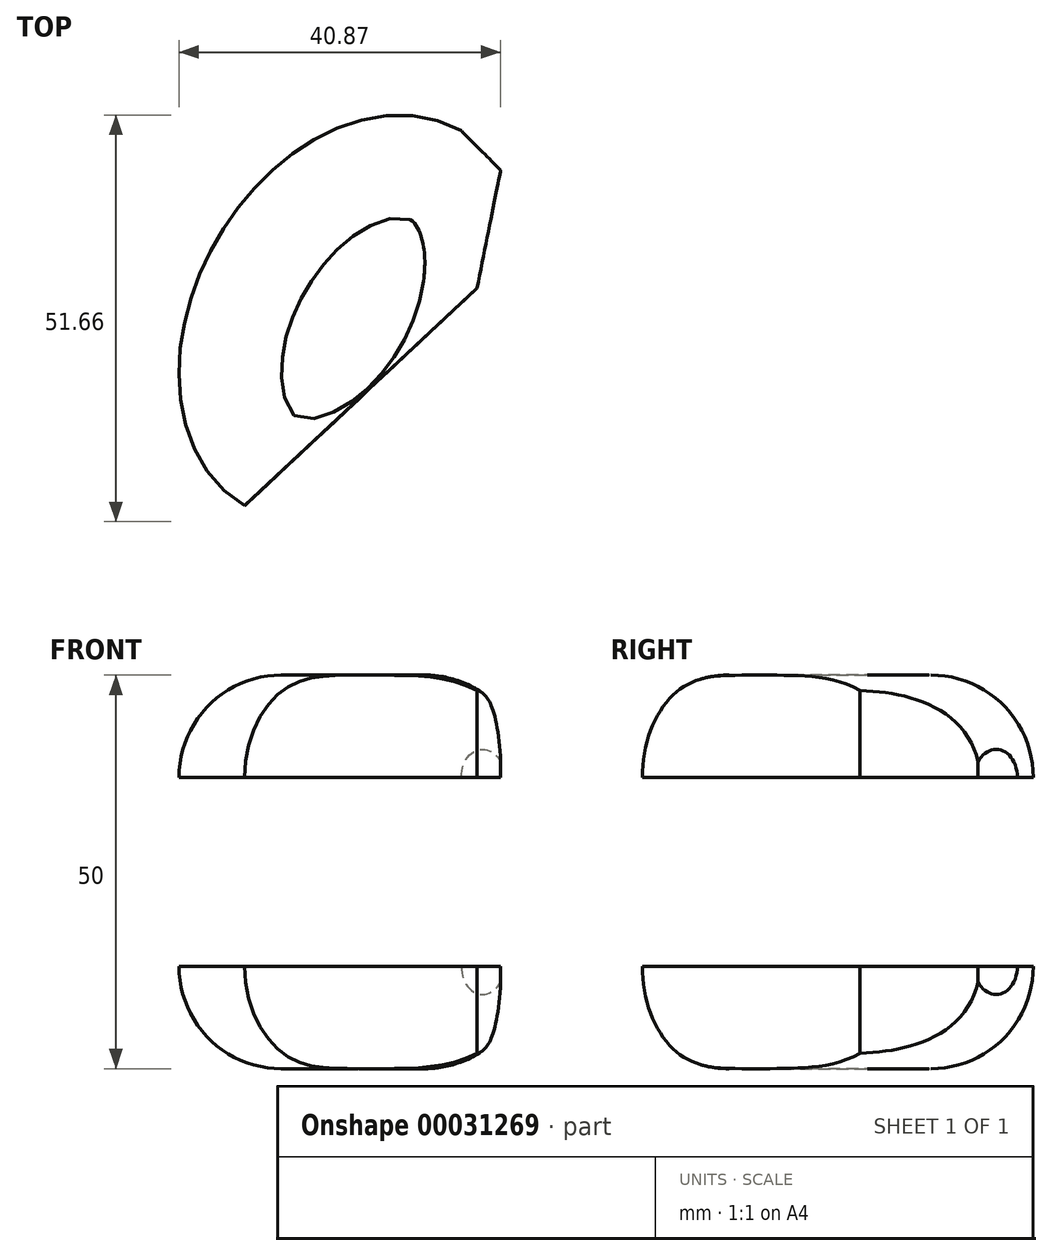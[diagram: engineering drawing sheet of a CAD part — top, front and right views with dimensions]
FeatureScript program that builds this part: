
annotation { "Feature Type Name" : "Feature", "Feature Type Description" : "" }
export const myFeature = defineFeature(function(context is Context, id is Id, definition is map)
    precondition{}
    {
        {
            var Q0;
            Q0=qCreatedBy(makeId("Top.planeOp"),FACE);
            var sketch = newSketch(context, id + "F0", { "sketchPlane" : qUnion([Q0])});
            skEllipticalArc(sketch, "E0", {});
            skPoint(sketch, "E1", {"position": v(13.75, 23.82) * mm});
            skPoint(sketch, "E2", {"position": v(-17.32, 10) * mm});
            skLineSegment(sketch, "E3", {"start": v(13.75, 23.82) * mm, "end": v(0, 0) * mm, "construction": true});
            skLineSegment(sketch, "E4", {"start": v(0, 0) * mm, "end": v(-13.75, -23.82) * mm, "construction": true});
            skLineSegment(sketch, "E5", {"start": v(13.75, 23.82) * mm, "end": v(18.75, 18.82) * mm});
            skLineSegment(sketch, "E6", {"start": v(18.75, 18.82) * mm, "end": v(15.75, 3.82) * mm});
            skLineSegment(sketch, "E7", {"start": v(15.75, 3.82) * mm, "end": v(-13.75, -23.82) * mm});
            const initialGuessF0  = {"E0": [0, 0, 0.5, 0.8660254037844386, 0.0275, 0.02, 0, 3.141592653589793]};
            skSetInitialGuess(sketch, initialGuessF0);
            skSolve(sketch);
        }
        {
            var Q0;
            Q0=qSketchRegion(id+"F0",true);
            extrude(context, id + "F1", {"entities" : qUnion([Q0]), "depth" : 25 * mm, "hasSecondDirection" : true, "secondDirectionOppositeDirection" : true, "secondDirectionDepth" : 25 * mm});
        }
        {
            var Q0;
            Q0=makeQuery(id+"F1.opExtrude","CAP_EDGE",EDGE,{"disambiguationData":[OSD([sQuery(id+"F0.wireOp",EDGE,"E0")])],"isStart":true});
            var Q1;
            Q1=makeQuery(id+"F1.opExtrude","CAP_EDGE",EDGE,{"disambiguationData":[OSD([sQuery(id+"F0.wireOp",EDGE,"E0")])],"isStart":false});
            fillet(context, id + "F2", {"entities" : qUnion([Q0, Q1]), "radius" : 13 * mm, "tangentPropagation" : true, "allowEdgeOverflow" : false});
        }
        {
            var Q0;
            Q0=qCreatedBy(makeId("Front.planeOp"),FACE);
            var sketch = newSketch(context, id + "F3", { "sketchPlane" : qUnion([Q0])});
            skLineSegment(sketch, "E8.0", {"start": v(18.75, 14.02) * mm, "end": v(18.75, -14.02) * mm, "construction": true});
            skFitSpline(sketch, "E9.0", {"points": [v(-9.11, -25) * mm, v(-3.04, -25) * mm, v(3.04, -25) * mm, v(9.11, -25) * mm], "construction": true});
            skLineSegment(sketch, "E10", {"start": v(-22.11, -12) * mm, "end": v(-22.11, 12) * mm, "construction": true});
            skLineSegment(sketch, "E11.bottom", {"start": v(18.75, 0) * mm, "end": v(-22.11, 0) * mm});
            skLineSegment(sketch, "E11.top", {"start": v(18.75, -25) * mm, "end": v(-22.11, -25) * mm});
            skLineSegment(sketch, "E11.left", {"start": v(18.75, 0) * mm, "end": v(18.75, -25) * mm});
            skLineSegment(sketch, "E11.right", {"start": v(-22.11, 0) * mm, "end": v(-22.11, -25) * mm});
            skLineSegment(sketch, "E12.bottom", {"start": v(-22.11, 0) * mm, "end": v(18.75, 0) * mm});
            skLineSegment(sketch, "E12.top", {"start": v(-22.11, 12) * mm, "end": v(18.75, 12) * mm});
            skLineSegment(sketch, "E12.left", {"start": v(-22.11, 0) * mm, "end": v(-22.11, 12) * mm});
            skLineSegment(sketch, "E12.right", {"start": v(18.75, 0) * mm, "end": v(18.75, 12) * mm});
            skSolve(sketch);
        }
        {
            var Q0;
            Q0 = qSketchRegion(id + "F3", true);
            extrude(context, id + "F4", {"entities" : qUnion([Q0]), "operationType" : NewBodyOperationType.REMOVE, "endBound" : BoundingType.THROUGH_ALL, "oppositeDirection" : true, "depth" : 25 * mm, "hasSecondDirection" : true, "secondDirectionBound" : SecondDirectionBoundingType.THROUGH_ALL, "secondDirectionOppositeDirection" : false, "secondDirectionDepth" : 25 * mm});
        }
        {
            var Q0;
            Q0=makeQuery(id+"F1.opExtrude","SWEPT_BODY",BODY,{"disambiguationData":[OSD([sQuery(id+"F0.wireOp",EDGE,"E0"),sQuery(id+"F0.wireOp",EDGE,"E5"),sQuery(id+"F0.wireOp",EDGE,"E6"),sQuery(id+"F0.wireOp",EDGE,"E7")])]});
            var Q1;
            Q1=qCreatedBy(makeId("Top.planeOp"),FACE);
            mirror(context, id + "F5", {"entities" : qUnion([Q0]), "mirrorPlane" : qUnion([Q1])});
        }
    });
